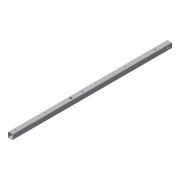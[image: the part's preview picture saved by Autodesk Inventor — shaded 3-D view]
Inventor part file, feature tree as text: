
AUTODESK INVENTOR PART (.ipt)
format: ipt  version: 2016 (Build 200138000, 138)  size: 224,768 bytes
history: native  units: in
note: dims shown in document units (in); Inventor stores cm internally (conversion verified against a paired STEP export)
features: sketch x7, hole x5, extrude x2
ambient origin geometry x8: Origin, YZ Plane, XZ Plane, XY Plane, X Axis, Y Axis, Z Axis, Center Point
bodies: Solid1 (feature_tree)
feature tree (14):
  extrude  "Extrusion1"  Depth=1.0in
  hole  "centerHole"  [1 undecoded]
  hole  "longSideHoles"  [1 undecoded]
  hole  "shortSideHoles"  [1 undecoded]
  hole  "shackleHole"  [1 undecoded]
  hole  "collarHole"  [1 undecoded]
  extrude  "removeSide"  Depth=1.0in
  sketch  "Sketch1"  dims[d0=1.0in d1=1.0in]
  sketch  "Sketch11"  dims[d2=0.125in d3=0.0787in]
  sketch  "Sketch12"  dims[d4=39.3701in d5=0.0in]
  sketch  "Sketch13"  dims[d69=0.4331in d70=0.75in d71=0.375in d72=0.25in d73=0.5635in d74=1.0in d75=0.8108in d76=0.125in]
  sketch  "Sketch14"  dims[d78=1.1811in d80=5.9055in d81=0.3937in d83=1.0in]
  sketch  "Sketch15"  dims[d85=0.2165in d86=0.75in d87=0.375in d88=0.25in d89=0.5635in d90=1.0in d91=0.8108in d94=1.1811in d96=6.0in d97=0.3937in d99=1.0in]
  sketch  "Sketch16"  dims[d101=0.2165in d102=0.75in d103=0.375in d104=0.25in d105=0.5635in d106=1.0in d107=0.8108in d108=0.375in d109=1.1811in d110=0.375in d111=0.7874in d112=0.315in d113=0.75in d114=0.375in d115=0.25in d116=0.5635in d117=1.0in d118=0.8108in d119=0.25in d120=2.3622in d128=0.2598in d129=0.75in d130=0.375in d131=0.25in d132=0.5635in d133=1.0in d134=0.8108in d135=7.6772in d136=0.0in d137=5.0in d138=6.0in d140=5.0in]
note: 5 required parameter values undecoded (feature->parameter linkage not recoverable at this tier; creation-order binding heuristic only, values carry confidence <= 0.55)
